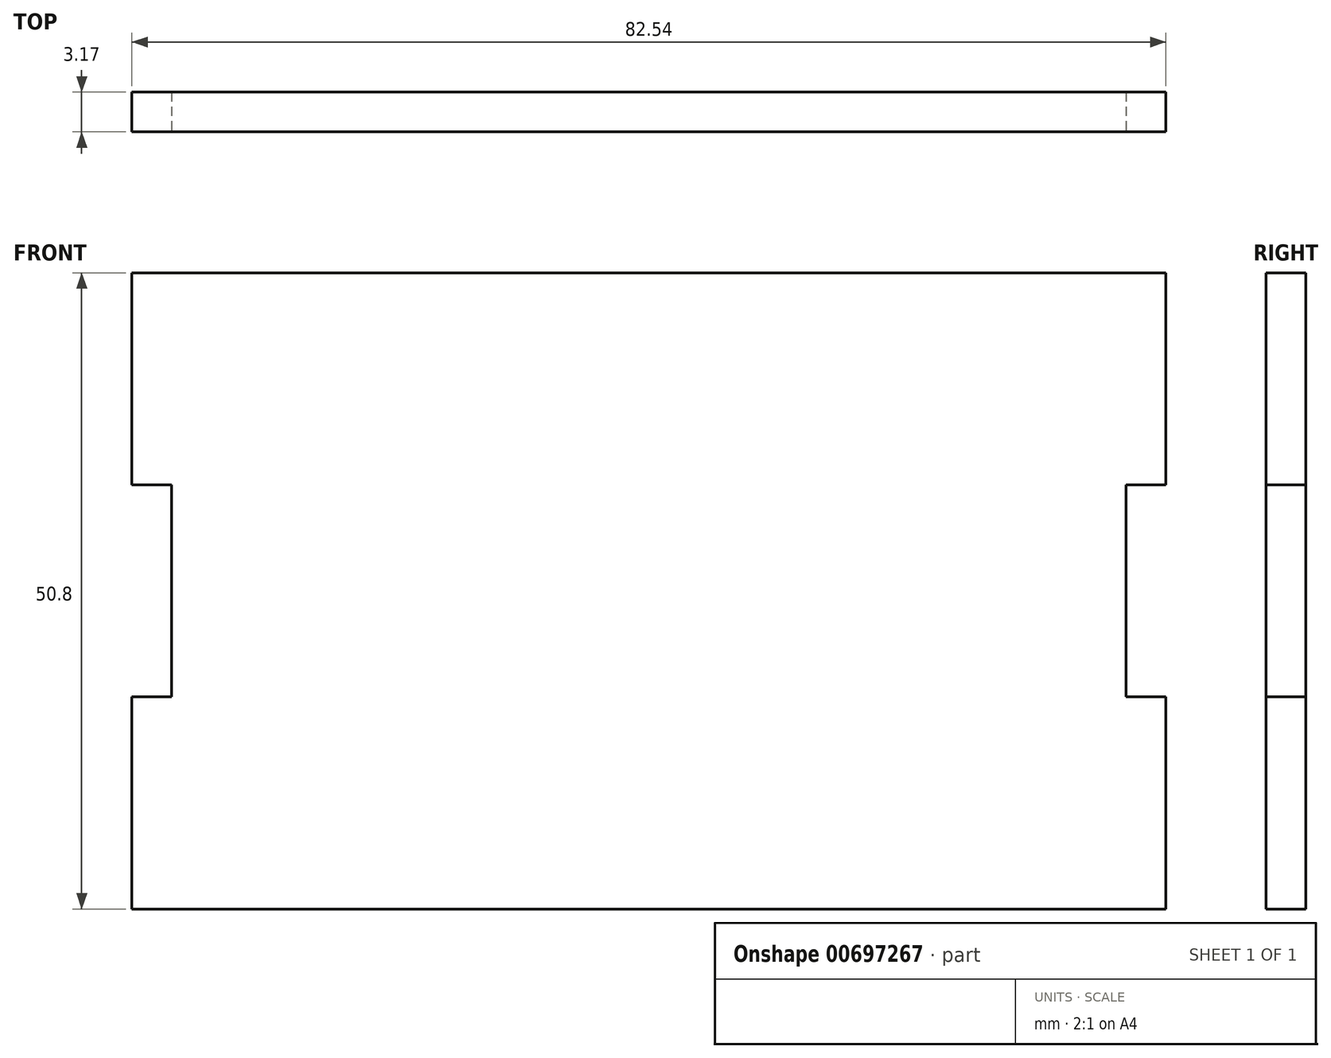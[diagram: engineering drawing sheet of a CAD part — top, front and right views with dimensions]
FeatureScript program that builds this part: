
annotation { "Feature Type Name" : "Feature", "Feature Type Description" : "" }
export const myFeature = defineFeature(function(context is Context, id is Id, definition is map)
    precondition{}
    {
        {
            var Q0;
            Q0=qCreatedBy(makeId("Front.planeOp"),FACE);
            var sketch = newSketch(context, id + "F0", { "sketchPlane" : qUnion([Q0])});
            skLineSegment(sketch, "E0.bottom", {"start": v(41.28, 25.4) * mm, "end": v(-41.28, 25.4) * mm});
            skLineSegment(sketch, "E0.top", {"start": v(41.28, -25.4) * mm, "end": v(-41.28, -25.4) * mm});
            skLineSegment(sketch, "E0.left", {"start": v(41.28, 25.4) * mm, "end": v(41.28, -25.4) * mm});
            skLineSegment(sketch, "E0.right", {"start": v(-41.28, 25.4) * mm, "end": v(-41.28, -25.4) * mm});
            skPoint(sketch, "E0.middle", {"position": v(0, 0) * mm});
            skSolve(sketch);
        }
        {
            var Q0;
            Q0=qSketchRegion(id+"F0",true);
            extrude(context, id + "F1", {"entities" : qUnion([Q0]), "depth" : 3.17 * mm, "offsetDistance" : 25.4 * mm});
        }
        {
            var Q0;
            Q0=makeQuery(id+"F1.opExtrude","CAP_FACE",FACE,{"disambiguationData":[OSD([sQuery(id+"F0.wireOp",EDGE,"E0.bottom"),sQuery(id+"F0.wireOp",EDGE,"E0.top"),sQuery(id+"F0.wireOp",EDGE,"E0.left"),sQuery(id+"F0.wireOp",EDGE,"E0.right")])],"isStart":false});
            var sketch = newSketch(context, id + "F2", { "sketchPlane" : qUnion([Q0])});
            skLineSegment(sketch, "E1", {"start": v(38.1, 25.4) * mm, "end": v(38.1, 8.47) * mm, "construction": true});
            skLineSegment(sketch, "E2", {"start": v(38.1, 8.47) * mm, "end": v(38.1, -8.47) * mm, "construction": true});
            skLineSegment(sketch, "E3", {"start": v(38.1, -8.47) * mm, "end": v(38.1, -25.4) * mm, "construction": true});
            skLineSegment(sketch, "E4.bottom", {"start": v(38.1, 8.47) * mm, "end": v(41.28, 8.47) * mm});
            skLineSegment(sketch, "E4.top", {"start": v(38.1, -8.47) * mm, "end": v(41.28, -8.47) * mm});
            skLineSegment(sketch, "E4.left", {"start": v(38.1, 8.47) * mm, "end": v(38.1, -8.47) * mm});
            skLineSegment(sketch, "E4.right", {"start": v(41.28, 8.47) * mm, "end": v(41.28, -8.47) * mm});
            skLineSegment(sketch, "E5", {"start": v(0, 25.4) * mm, "end": v(0, -25.4) * mm, "construction": true});
            skLineSegment(sketch, "E6.MirrorCS", {"start": v(-38.1, 8.47) * mm, "end": v(-41.28, 8.47) * mm});
            skLineSegment(sketch, "E7.MirrorCS", {"start": v(-38.1, 8.47) * mm, "end": v(-38.1, -8.47) * mm, "construction": true});
            skLineSegment(sketch, "E8.MirrorCS", {"start": v(-41.28, 8.47) * mm, "end": v(-41.28, -8.47) * mm});
            skLineSegment(sketch, "E9.MirrorCS", {"start": v(-38.1, -8.47) * mm, "end": v(-41.28, -8.47) * mm});
            skLineSegment(sketch, "E10", {"start": v(-38.1, 8.47) * mm, "end": v(-38.1, -8.47) * mm});
            skSolve(sketch);
        }
        {
            var Q0;
            Q0=makeQuery(id+"F2.imprint","IMPRINT",FACE,{"disambiguationData":[TD([[makeQuery(id+"F2.imprint","IMPRINT",EDGE,{"derivedFrom":sQuery(id+"F2.wireOp",EDGE,"E4.bottom")}),-1.0]])]});
            var Q1;
            Q1=makeQuery(id+"F2.imprint","IMPRINT",FACE,{"disambiguationData":[TD([[makeQuery(id+"F2.imprint","IMPRINT",EDGE,{"derivedFrom":sQuery(id+"F2.wireOp",EDGE,"E6.MirrorCS")}),1.0]])]});
            extrude(context, id + "F3", {"entities" : qUnion([Q0, Q1]), "operationType" : NewBodyOperationType.REMOVE, "oppositeDirection" : true, "depth" : 3.17 * mm, "offsetDistance" : 25.4 * mm});
        }
    });
